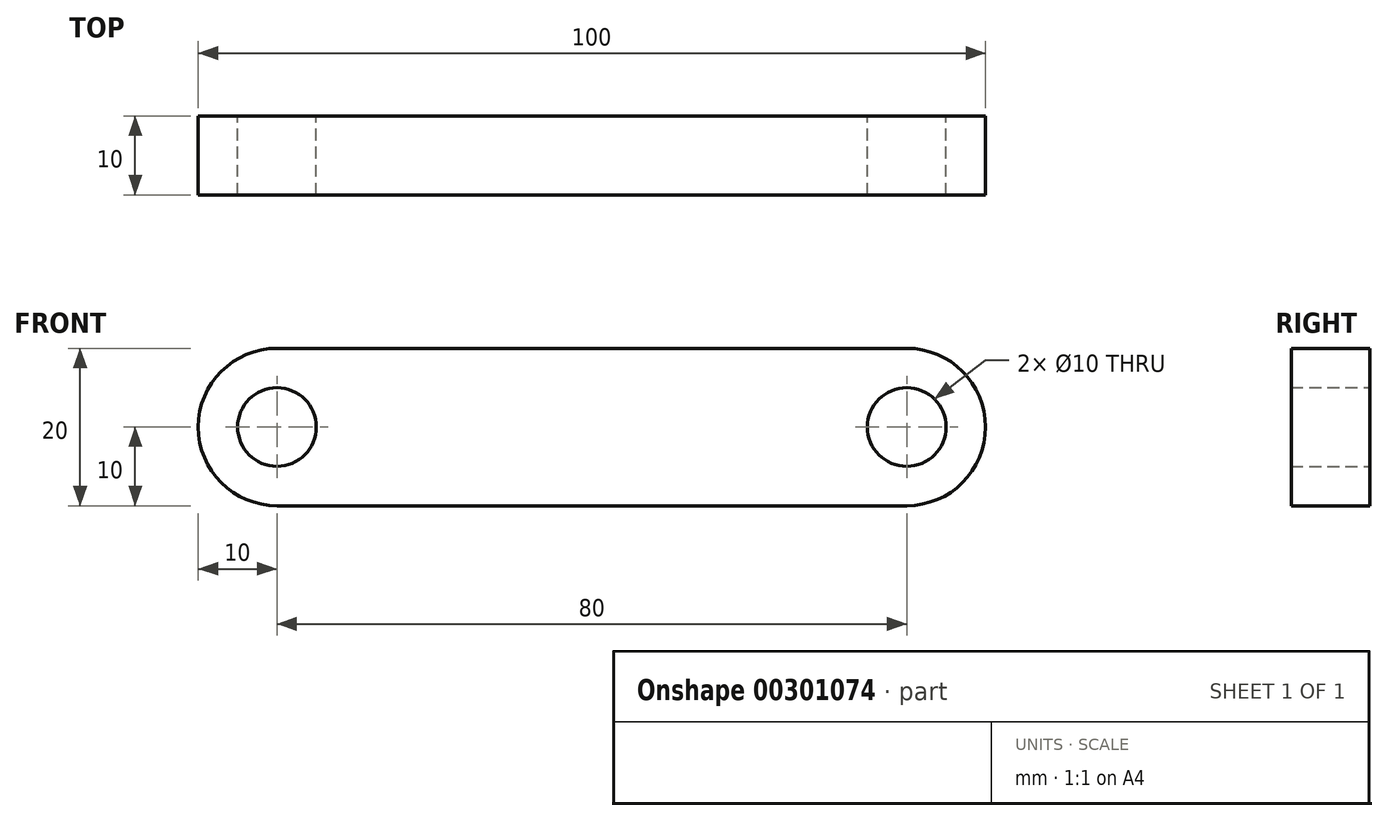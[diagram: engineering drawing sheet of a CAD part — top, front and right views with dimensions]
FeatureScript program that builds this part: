
annotation { "Feature Type Name" : "Feature", "Feature Type Description" : "" }
export const myFeature = defineFeature(function(context is Context, id is Id, definition is map)
    precondition{}
    {
        {
            var Q0;
            Q0=qCreatedBy(makeId("Front.planeOp"),FACE);
            var sketch = newSketch(context, id + "F0", { "sketchPlane" : qUnion([Q0])});
            skLineSegment(sketch, "E0", {"start": v(0, 0) * mm, "end": v(80, 0) * mm});
            skLineSegment(sketch, "E1", {"start": v(80, 20) * mm, "end": v(0, 20) * mm});
            skArc(sketch, "E2", {"start": v(0, 20) * mm, "mid": v(-10, 10) * mm, "end": v(0, 0) * mm});
            skArc(sketch, "E3", {"start": v(80, 20) * mm, "mid": v(90, 10) * mm, "end": v(80, 0) * mm});
            skCircle(sketch, "E4", {"center": v(0, 10) * mm, "radius": 5 * mm});
            skCircle(sketch, "E5", {"center": v(80, 10) * mm, "radius": 5 * mm});
            skSolve(sketch);
        }
        {
            var Q0;
            Q0 = qSketchRegion(id + "F0", true);
            extrude(context, id + "F1", {"entities" : qUnion([Q0]), "depth" : 10 * mm});
        }
    });
